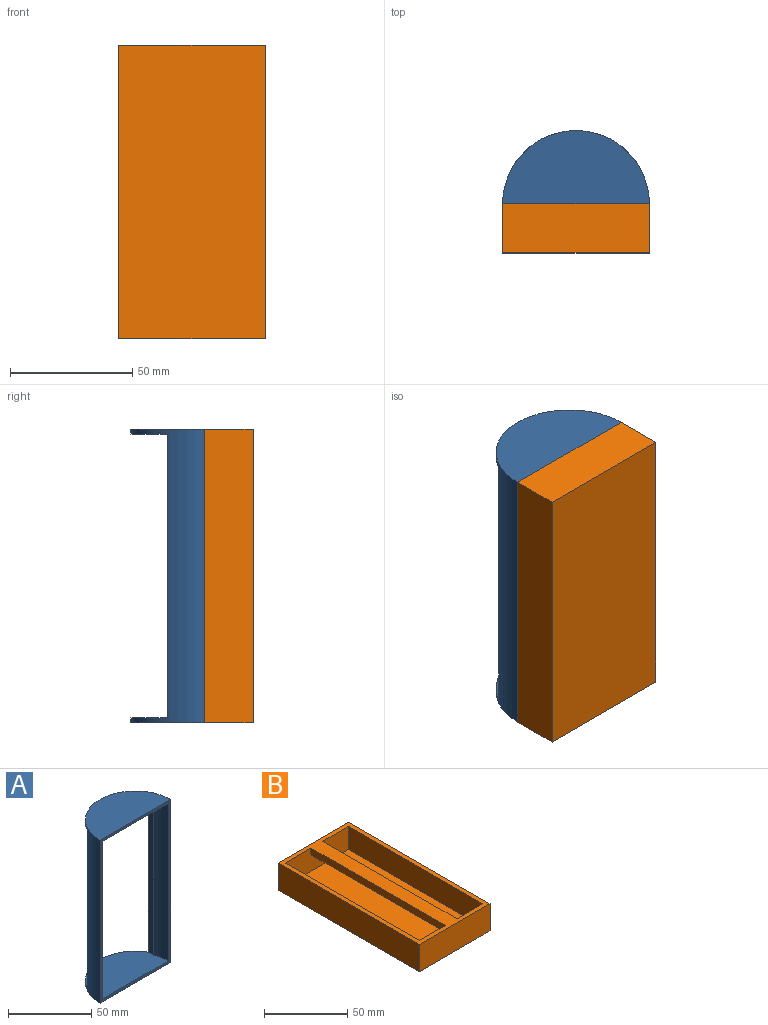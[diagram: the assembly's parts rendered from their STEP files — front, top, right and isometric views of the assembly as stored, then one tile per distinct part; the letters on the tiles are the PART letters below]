
ASSEMBLY  parts=2 mates=1
PART A: 10 faces, bbox 60x30x120 mm
  f0: cylinder r=30mm len=120mm, axis (0,0,-1), area 4012.3mm2, adj f2,f3,f4,f6,f7,f8,f9
  f1: cylinder r=28mm len=116mm, axis (0,0,-1), area 1235.1mm2, adj f2,f6,f7,f9
  f2: plane 120x60mm, normal (0,-1,0), area 704mm2, adj f0,f1,f3,f4,f5,f6,f7
  f3: plane 60x30mm, normal (0,0,1), area 1413.7mm2, adj f0,f2
  f4: plane 60x30mm, normal (0,0,-1), area 1413.7mm2, adj f0,f2
  f5: cylinder r=28mm len=116mm, axis (0,0,-1), area 1235.1mm2, adj f2,f6,f7,f8
  f6: plane 56x30mm, normal (0,0,-1), area 1360.7mm2, adj f0,f1,f2,f5,f8,f9
  f7: plane 56x30mm, normal (0,0,1), area 1360.7mm2, adj f0,f1,f2,f5,f8,f9
  f8: plane 116x4.57mm, normal (1,0,0), area 530.6mm2, adj f0,f5,f6,f7
  f9: plane 116x4.57mm, normal (-1,0,0), area 530.6mm2, adj f0,f1,f6,f7
PART B: 14 faces, bbox 60x120x20 mm
  f0: plane 54x17mm, normal (0,-1,0), area 868mm2, adj f1,f7,f9,f10,f11,f12,f13
  f1: plane 120x60mm, normal (0,0,1), area 2184mm2, adj f0,f2,f3,f4,f5,f7,f8,f9
  f2: plane 60x20mm, normal (0,1,0), area 1200mm2, adj f1,f3,f5,f6
  f3: plane 120x20mm, normal (-1,0,0), area 2400mm2, adj f1,f2,f4,f6
  f4: plane 60x20mm, normal (0,-1,0), area 1200mm2, adj f1,f3,f5,f6
  f5: plane 120x20mm, normal (1,0,0), area 2400mm2, adj f1,f2,f4,f6
  f6: plane 120x60mm, normal (0,0,-1), area 7200mm2, adj f2,f3,f4,f5
  f7: plane 114x17mm, normal (1,0,0), area 1938mm2, adj f0,f1,f8,f10
  f8: plane 54x17mm, normal (0,1,0), area 868mm2, adj f1,f7,f9,f10,f11,f12,f13
  f9: plane 114x17mm, normal (-1,0,0), area 1938mm2, adj f0,f1,f8,f10
  f10: plane 114x54mm, normal (0,0,1), area 6156mm2, adj f0,f7,f8,f9
  f11: plane 114x5mm, normal (1,0,0), area 570mm2, adj f0,f1,f8,f13
  f12: plane 114x5mm, normal (-1,0,0), area 570mm2, adj f0,f1,f8,f13
  f13: plane 114x10mm, normal (0,0,-1), area 1140mm2, adj f0,f8,f11,f12
PLACE A t=(25.16,-22.01,3.07)mm
PLACE B rot(axis=(0,0.71,0.71),180deg) t=(25.16,-42.01,3.07)mm
MATE fastened B.f1 <-> A.f2  axis (0,1,0) through (25.16,-22.01,63.07)mm
